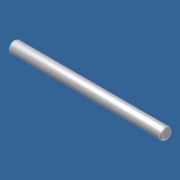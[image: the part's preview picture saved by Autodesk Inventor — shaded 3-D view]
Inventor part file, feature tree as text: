
AUTODESK INVENTOR PART (.ipt)
format: ipt  version: unknown  size: 168,960 bytes
history: native  units: in
note: dims shown in document units (in); Inventor stores cm internally (conversion verified against a paired STEP export)
features: revolve x1, fillet x1, sketch x1
ambient origin geometry x8: Origin, YZ Plane, XZ Plane, XY Plane, X Axis, Y Axis, Z Axis, Center Point
bodies: Solid1 (feature_tree)
feature tree (3):
  revolve  "Revolution1"  [1 undecoded]
  fillet  "Fillet1"  [1 undecoded]
  sketch  "Sketch1"  dims[d0=2.5in d1=0.094in d2=90.0deg d3=0.0313in]
note: 2 required parameter values undecoded (feature->parameter linkage not recoverable at this tier; creation-order binding heuristic only, values carry confidence <= 0.55)